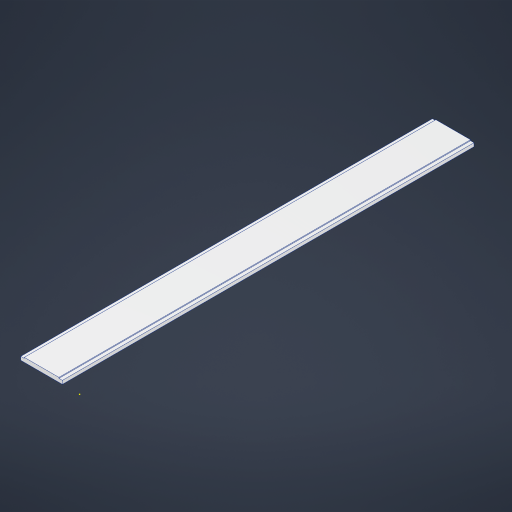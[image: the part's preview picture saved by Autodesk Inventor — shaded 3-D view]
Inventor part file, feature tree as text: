
AUTODESK INVENTOR PART (.ipt)
format: ipt  version: 2024 (Build 280153000, 153)  size: 193,024 bytes
history: native  units: mm
features: sketch x3, extrude x2
ambient origin geometry x8: Origin, YZ Plane, XZ Plane, XY Plane, X Axis, Y Axis, Z Axis, Center Point
bodies: Solid1 (feature_tree)
feature tree (5):
  extrude  "Extrusion1"  Depth=96.0mm
  sketch  "Sketch2"  dims[d2=14.0mm d3=0.0mm d4=8.0mm]
  extrude  "Extrusion2"  Depth=8.0mm
  sketch  "Sketch1"  dims[d0=950.0mm d1=96.0mm]
  sketch  "Sketch3"  dims[d5=6.0mm d6=6.0mm d7=0.0mm d8=0.0mm]
